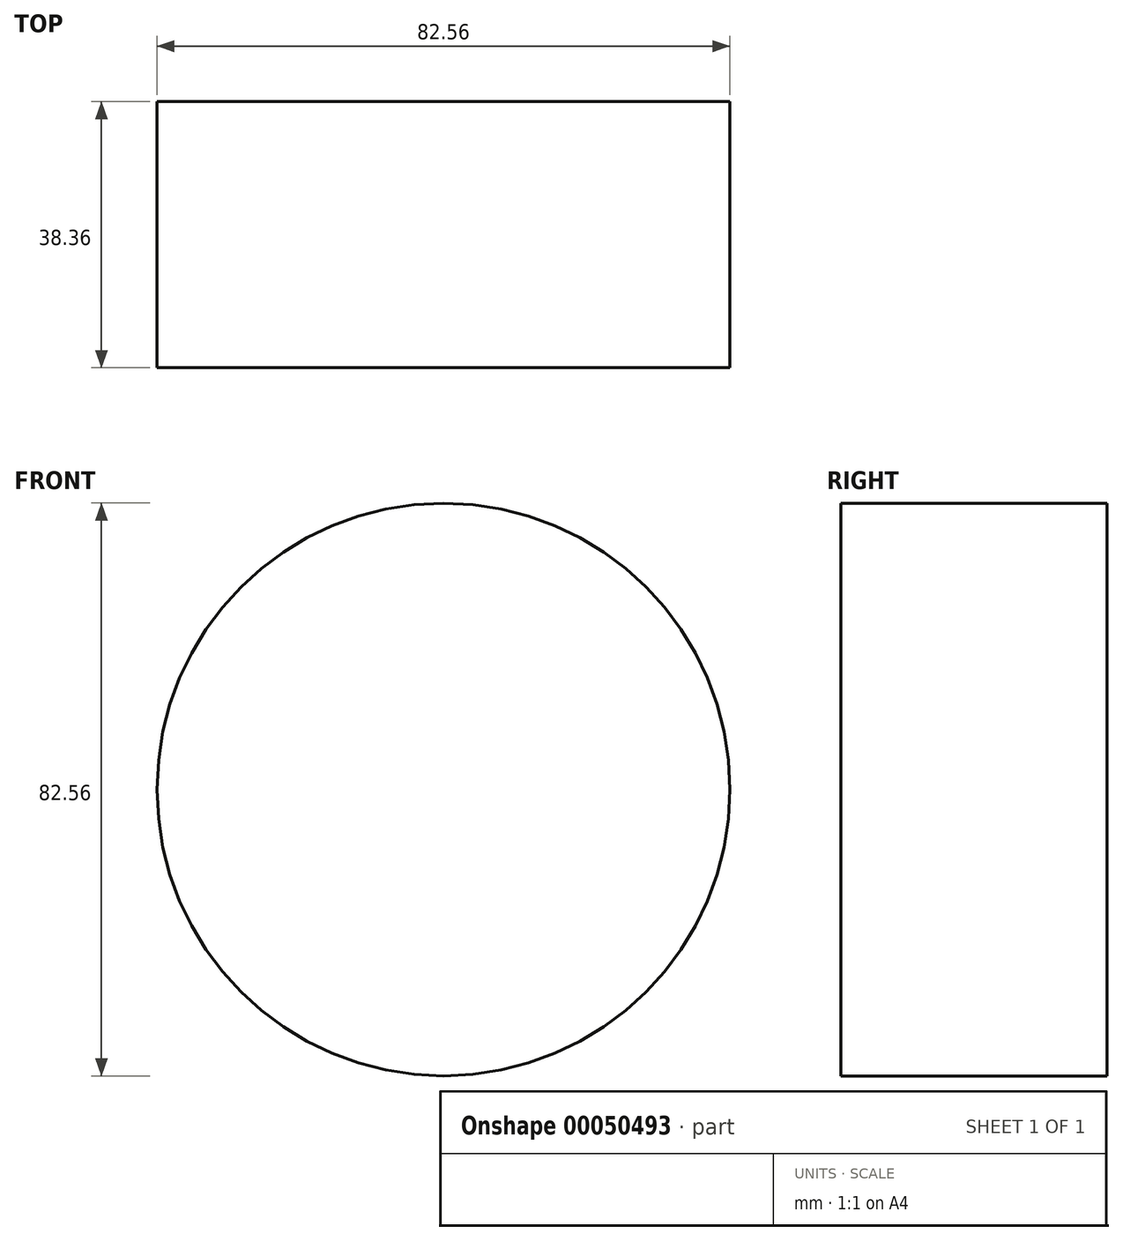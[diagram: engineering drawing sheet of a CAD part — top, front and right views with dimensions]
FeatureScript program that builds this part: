
annotation { "Feature Type Name" : "Feature", "Feature Type Description" : "" }
export const myFeature = defineFeature(function(context is Context, id is Id, definition is map)
    precondition{}
    {
        {
            var Q0;
            Q0=qCreatedBy(makeId("Front.planeOp"),FACE);
            var sketch = newSketch(context, id + "F0", { "sketchPlane" : qUnion([Q0])});
            skCircle(sketch, "E0", {"center": v(0, 0) * mm, "radius": 41.28 * mm});
            skSolve(sketch);
        }
        {
            var Q0;
            Q0 = qSketchRegion(id + "F0", true);
            extrude(context, id + "F1", {"entities" : qUnion([Q0]), "endBound" : BoundingType.SYMMETRIC, "depth" : 38.35 * mm});
        }
    });
